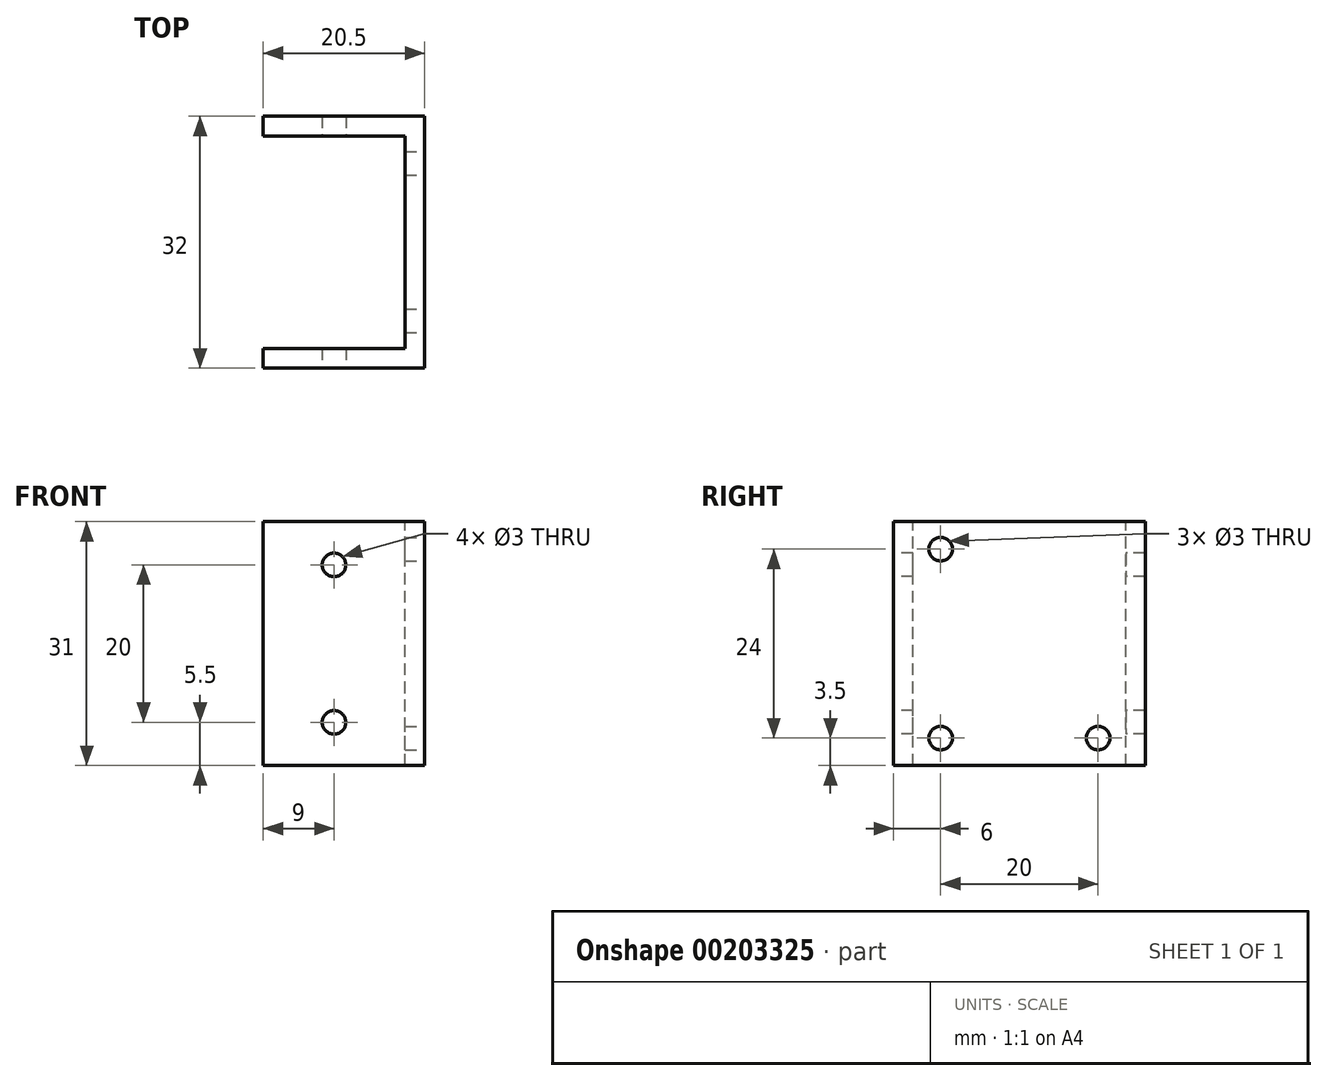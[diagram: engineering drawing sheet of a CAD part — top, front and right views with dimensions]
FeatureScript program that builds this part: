
annotation { "Feature Type Name" : "Feature", "Feature Type Description" : "" }
export const myFeature = defineFeature(function(context is Context, id is Id, definition is map)
    precondition{}
    {
        {
            var Q0;
            Q0=qCreatedBy(makeId("Right.planeOp"),FACE);
            var sketch = newSketch(context, id + "F0", { "sketchPlane" : qUnion([Q0])});
            skLineSegment(sketch, "E0.bottom", {"start": v(13.5, -15.5) * mm, "end": v(-13.5, -15.5) * mm});
            skLineSegment(sketch, "E0.top", {"start": v(13.5, 15.5) * mm, "end": v(-13.5, 15.5) * mm});
            skLineSegment(sketch, "E0.left", {"start": v(13.5, -15.5) * mm, "end": v(13.5, 15.5) * mm});
            skLineSegment(sketch, "E0.right", {"start": v(-13.5, -15.5) * mm, "end": v(-13.5, 15.5) * mm});
            skPoint(sketch, "E0.middle", {"position": v(0, 0) * mm});
            skSolve(sketch);
        }
        {
            var Q0;
            Q0 = qSketchRegion(id + "F0", true);
            extrude(context, id + "F1", {"entities" : qUnion([Q0]), "depth" : 2.5 * mm});
        }
        {
            var Q0;
            Q0=makeQuery(id+"F1.opExtrude","SWEPT_FACE",FACE,{"disambiguationData":[OSD([sQuery(id+"F0.wireOp",EDGE,"E0.left")])]});
            var sketch = newSketch(context, id + "F2", { "sketchPlane" : qUnion([Q0])});
            skLineSegment(sketch, "E1.bottom", {"start": v(-2.5, 15.5) * mm, "end": v(18, 15.5) * mm});
            skLineSegment(sketch, "E1.top", {"start": v(-2.5, -15.5) * mm, "end": v(18, -15.5) * mm});
            skLineSegment(sketch, "E1.left", {"start": v(-2.5, 15.5) * mm, "end": v(-2.5, -15.5) * mm});
            skLineSegment(sketch, "E1.right", {"start": v(18, 15.5) * mm, "end": v(18, -15.5) * mm});
            skSolve(sketch);
        }
        {
            var Q0;
            Q0 = qSketchRegion(id + "F2", true);
            extrude(context, id + "F3", {"entities" : qUnion([Q0]), "operationType" : NewBodyOperationType.ADD, "depth" : 2.5 * mm});
        }
        {
            var Q0;
            Q0=makeQuery(id+"F1.opExtrude","SWEPT_FACE",FACE,{"disambiguationData":[OSD([sQuery(id+"F0.wireOp",EDGE,"E0.right")])]});
            var sketch = newSketch(context, id + "F4", { "sketchPlane" : qUnion([Q0])});
            skLineSegment(sketch, "E2.bottom", {"start": v(2.5, -15.5) * mm, "end": v(-18, -15.5) * mm});
            skLineSegment(sketch, "E2.top", {"start": v(2.5, 15.5) * mm, "end": v(-18, 15.5) * mm});
            skLineSegment(sketch, "E2.left", {"start": v(2.5, -15.5) * mm, "end": v(2.5, 15.5) * mm});
            skLineSegment(sketch, "E2.right", {"start": v(-18, -15.5) * mm, "end": v(-18, 15.5) * mm});
            skSolve(sketch);
        }
        {
            var Q0;
            Q0 = qSketchRegion(id + "F4", true);
            extrude(context, id + "F5", {"entities" : qUnion([Q0]), "operationType" : NewBodyOperationType.ADD, "depth" : 2.5 * mm});
        }
        {
            var Q0;
            Q0=makeQuery(id+"F5.boolean.opBoolean","MERGE",FACE,{"derivedFrom":[makeQuery(id+"F3.boolean.opBoolean","MERGE",FACE,{"derivedFrom":[makeQuery(id+"F1.opExtrude","CAP_FACE",FACE,{"disambiguationData":[OSD([sQuery(id+"F0.wireOp",EDGE,"E0.bottom"),sQuery(id+"F0.wireOp",EDGE,"E0.top"),sQuery(id+"F0.wireOp",EDGE,"E0.left"),sQuery(id+"F0.wireOp",EDGE,"E0.right")])],"isStart":false}),makeQuery(id+"F3.opExtrude","SWEPT_FACE",FACE,{"disambiguationData":[OSD([sQuery(id+"F2.wireOp",EDGE,"E1.left")])]})]}),makeQuery(id+"F5.opExtrude","SWEPT_FACE",FACE,{"disambiguationData":[OSD([sQuery(id+"F4.wireOp",EDGE,"E2.left")])]})]});
            var sketch = newSketch(context, id + "F6", { "sketchPlane" : qUnion([Q0])});
            skLineSegment(sketch, "E3", {"start": v(-16, 0) * mm, "end": v(16, 0) * mm, "construction": true});
            skLineSegment(sketch, "E4", {"start": v(0, 15.5) * mm, "end": v(0, -15.5) * mm, "construction": true});
            skLineSegment(sketch, "E5", {"start": v(-16, -12) * mm, "end": v(16, -12) * mm, "construction": true});
            skCircle(sketch, "E6", {"center": v(-10, -12) * mm, "radius": 1.5 * mm});
            skCircle(sketch, "E7.MirrorC", {"center": v(-10, 12) * mm, "radius": 1.5 * mm});
            skCircle(sketch, "E8.MirrorC", {"center": v(10, -12) * mm, "radius": 1.5 * mm});
            skSolve(sketch);
        }
        {
            var Q0;
            Q0 = qSketchRegion(id + "F6", true);
            extrude(context, id + "F7", {"entities" : qUnion([Q0]), "operationType" : NewBodyOperationType.REMOVE, "endBound" : BoundingType.THROUGH_ALL, "oppositeDirection" : true, "depth" : 25 * mm});
        }
        {
            var Q0;
            Q0=makeQuery(id+"F5.opExtrude","CAP_FACE",FACE,{"disambiguationData":[OSD([sQuery(id+"F4.wireOp",EDGE,"E2.bottom"),sQuery(id+"F4.wireOp",EDGE,"E2.top"),sQuery(id+"F4.wireOp",EDGE,"E2.left"),sQuery(id+"F4.wireOp",EDGE,"E2.right")])],"isStart":false});
            var sketch = newSketch(context, id + "F8", { "sketchPlane" : qUnion([Q0])});
            skLineSegment(sketch, "E9", {"start": v(-18, 0) * mm, "end": v(2.5, 0) * mm, "construction": true});
            skPoint(sketch, "E10.endSnap0", {"position": v(-7.75, -15.5) * mm});
            skCircle(sketch, "E11", {"center": v(-9, 10) * mm, "radius": 1.5 * mm});
            skCircle(sketch, "E12.MirrorC", {"center": v(-9, -10) * mm, "radius": 1.5 * mm});
            skLineSegment(sketch, "E13", {"start": v(0, 15.5) * mm, "end": v(0, -15.5) * mm, "construction": true});
            skLineSegment(sketch, "E14", {"start": v(-9, 15.5) * mm, "end": v(-9, -15.5) * mm, "construction": true});
            skSolve(sketch);
        }
        {
            var Q0;
            Q0 = qSketchRegion(id + "F8", true);
            extrude(context, id + "F9", {"entities" : qUnion([Q0]), "operationType" : NewBodyOperationType.REMOVE, "endBound" : BoundingType.THROUGH_ALL, "oppositeDirection" : true, "depth" : 25 * mm});
        }
    });
